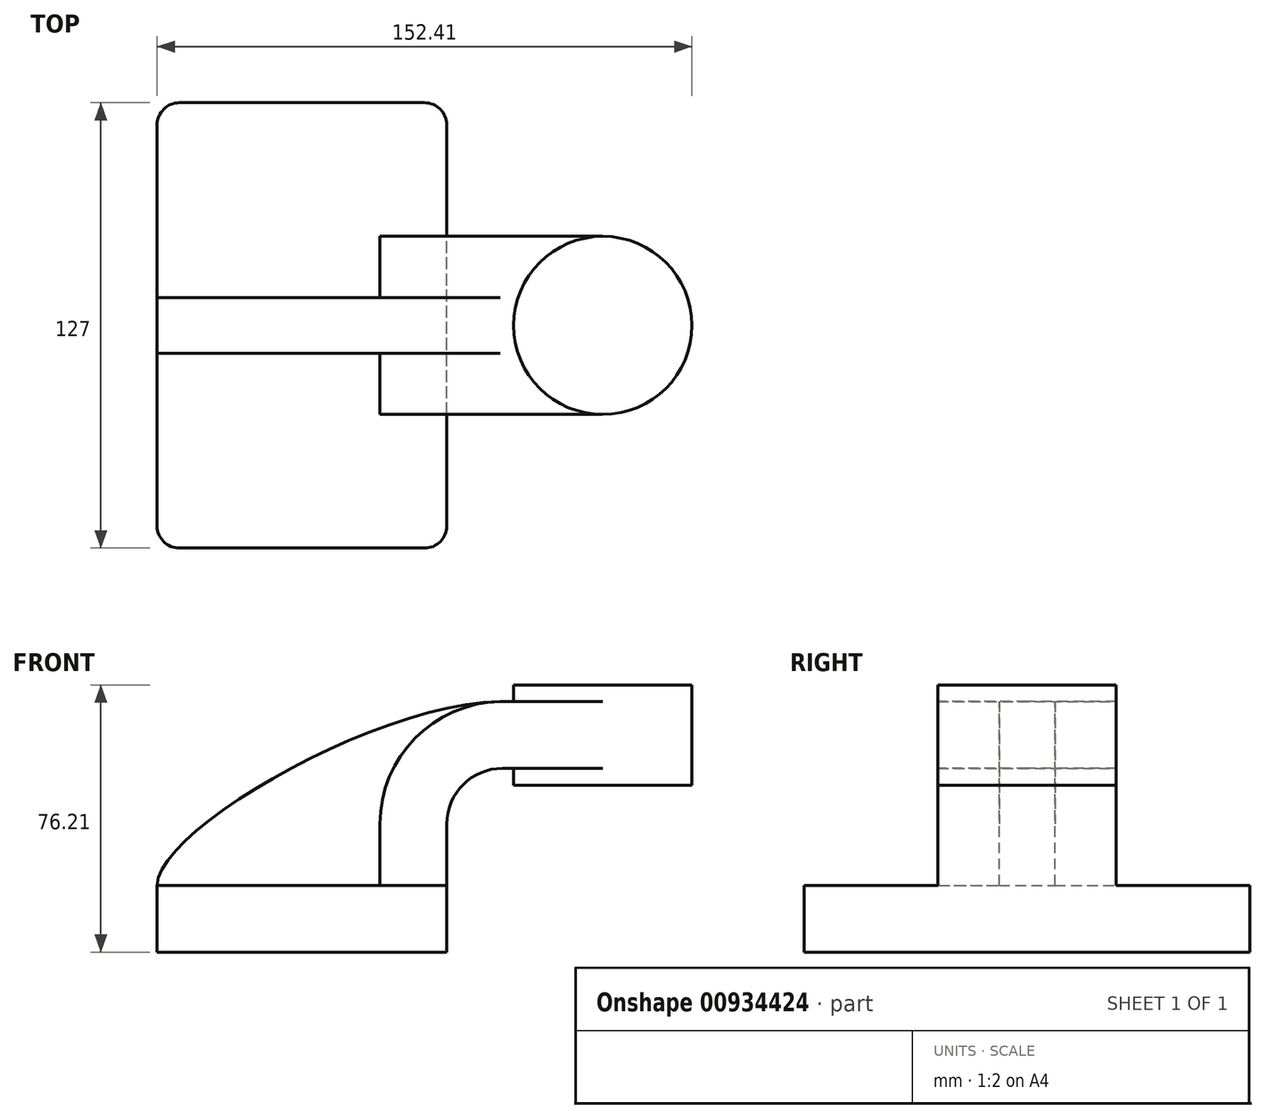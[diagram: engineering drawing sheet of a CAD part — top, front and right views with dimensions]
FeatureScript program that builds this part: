
annotation { "Feature Type Name" : "Feature", "Feature Type Description" : "" }
export const myFeature = defineFeature(function(context is Context, id is Id, definition is map)
    precondition{}
    {
        {
            var Q0;
            Q0=qCreatedBy(makeId("Front.planeOp"),FACE);
            var sketch = newSketch(context, id + "F0", { "sketchPlane" : qUnion([Q0])});
            skLineSegment(sketch, "E0.bottom", {"start": v(-41.28, 9.53) * mm, "end": v(41.27, 9.53) * mm});
            skLineSegment(sketch, "E0.top", {"start": v(-41.28, -9.53) * mm, "end": v(41.28, -9.53) * mm});
            skLineSegment(sketch, "E0.left", {"start": v(-41.27, 9.52) * mm, "end": v(-41.27, -9.53) * mm});
            skLineSegment(sketch, "E0.right", {"start": v(41.27, 9.53) * mm, "end": v(41.27, -9.52) * mm});
            skPoint(sketch, "E0.middle", {"position": v(0, 0) * mm});
            skLineSegment(sketch, "E1", {"start": v(41.28, 9.53) * mm, "end": v(41.28, 27) * mm});
            skArc(sketch, "E2", {"start": v(41.27, 27) * mm, "mid": v(45.92, 38.23) * mm, "end": v(57.15, 42.88) * mm});
            skLineSegment(sketch, "E3.bottom", {"start": v(111.12, 66.67) * mm, "end": v(60.32, 66.67) * mm});
            skLineSegment(sketch, "E3.top", {"start": v(111.12, 38.1) * mm, "end": v(60.32, 38.1) * mm});
            skLineSegment(sketch, "E3.left", {"start": v(111.12, 66.67) * mm, "end": v(111.12, 38.1) * mm});
            skLineSegment(sketch, "E3.right", {"start": v(60.32, 66.67) * mm, "end": v(60.32, 38.1) * mm});
            skPoint(sketch, "E3.middle", {"position": v(85.72, 52.39) * mm});
            skLineSegment(sketch, "E4", {"start": v(57.15, 42.88) * mm, "end": v(85.72, 42.88) * mm});
            skLineSegment(sketch, "E5.0", {"start": v(57.15, 61.93) * mm, "end": v(85.72, 61.93) * mm});
            skArc(sketch, "E5.1", {"start": v(22.22, 27) * mm, "mid": v(32.45, 51.7) * mm, "end": v(57.15, 61.93) * mm});
            skLineSegment(sketch, "E5.2", {"start": v(22.23, 9.53) * mm, "end": v(22.23, 27) * mm});
            skLineSegment(sketch, "E6", {"start": v(85.72, 38.1) * mm, "end": v(85.72, 66.67) * mm});
            skFitSpline(sketch, "E7", {"points": [v(-41.28, 9.52) * mm, v(57.15, 61.93) * mm], "startDerivative": vector(0.6, 47.75) * mm, "endDerivative": vector(106.9, 0.34) * mm});
            skSolve(sketch);
        }
        {
            var Q0;
            Q0=makeQuery(id+"F0.imprint","IMPRINT",FACE,{"disambiguationData":[TD([[makeQuery(id+"F0.imprint","IMPRINT",EDGE,{"derivedFrom":sQuery(id+"F0.wireOp",EDGE,"E0.top")}),1.0]])]});
            extrude(context, id + "F1", {"entities" : qUnion([Q0]), "endBound" : BoundingType.SYMMETRIC, "depth" : 127 * mm, "offsetDistance" : 25.4 * mm});
        }
        {
            var Q0;
            {var subQ5=sQuery(id+"F0.wireOp",EDGE,"E1");Q0=makeQuery(id+"F0.imprint","IMPRINT",FACE,{"disambiguationData":[TD([[makeQuery(id+"F0.imprint","IMPRINT",EDGE,{"derivedFrom":subQ5}),1.0]])]});}
            extrude(context, id + "F2", {"entities" : qUnion([Q0]), "operationType" : NewBodyOperationType.ADD, "endBound" : BoundingType.SYMMETRIC, "depth" : 50.8 * mm, "offsetDistance" : 25.4 * mm});
        }
        {
            var Q0;
            {var subQ0=sQuery(id+"F0.wireOp",EDGE,"E5.0");var subQ1=sQuery(id+"F0.wireOp",EDGE,"E3.right");var subQ2=makeQuery(id+"F0.imprint","INTERSECT",VERTEX,{"derivedFrom":[subQ1,subQ0]});Q0=makeQuery(id+"F0.imprint","IMPRINT",FACE,{"disambiguationData":[TD([[makeQuery(id+"F0.imprint","IMPRINT",EDGE,{"disambiguationData":[TD([[subQ2,-1.0]])],"derivedFrom":subQ1}),1.0]])]});}
            extrude(context, id + "F3", {"entities" : qUnion([Q0]), "operationType" : NewBodyOperationType.ADD, "endBound" : BoundingType.SYMMETRIC, "depth" : 50.8 * mm, "offsetDistance" : 25.4 * mm});
        }
        {
            var Q0;
            {var subQ3=sQuery(id+"F0.wireOp",EDGE,"E5.2");Q0=makeQuery(id+"F0.imprint","IMPRINT",FACE,{"disambiguationData":[TD([[makeQuery(id+"F0.imprint","IMPRINT",EDGE,{"derivedFrom":subQ3}),1.0]])]});}
            extrude(context, id + "F4", {"entities" : qUnion([Q0]), "operationType" : NewBodyOperationType.ADD, "endBound" : BoundingType.SYMMETRIC, "depth" : 15.88 * mm, "offsetDistance" : 25.4 * mm});
        }
        {
            var Q0;
            {var subQ0=sQuery(id+"F0.wireOp",EDGE,"E3.left");Q0=makeQuery(id+"F0.imprint","IMPRINT",FACE,{"disambiguationData":[TD([[makeQuery(id+"F0.imprint","IMPRINT",EDGE,{"derivedFrom":subQ0}),-1.0]])]});}
            var Q1;
            Q1=sQuery(id+"F0.wireOp",EDGE,"E6");
            revolve(context, id + "F5", {"operationType" : NewBodyOperationType.ADD, "surfaceOperationType" : NewSurfaceOperationType.NEW, "entities" : qUnion([Q0]), "axis" : qUnion([Q1]), "revolveType" : RevolveType.FULL});
        }
        {
            var Q0;
            Q0=makeQuery(id+"F1.opExtrude","CAP_EDGE",EDGE,{"disambiguationData":[OSD([sQuery(id+"F0.wireOp",EDGE,"E0.left")])],"isStart":false});
            var Q1;
            Q1=makeQuery(id+"F1.opExtrude","CAP_EDGE",EDGE,{"disambiguationData":[OSD([sQuery(id+"F0.wireOp",EDGE,"E0.right")])],"isStart":false});
            var Q2;
            Q2=makeQuery(id+"F1.opExtrude","CAP_EDGE",EDGE,{"disambiguationData":[OSD([sQuery(id+"F0.wireOp",EDGE,"E0.right")])],"isStart":true});
            var Q3;
            Q3=makeQuery(id+"F1.opExtrude","CAP_EDGE",EDGE,{"disambiguationData":[OSD([sQuery(id+"F0.wireOp",EDGE,"E0.left")])],"isStart":true});
            fillet(context, id + "F6", {"entities" : qUnion([Q0, Q1, Q2, Q3]), "radius" : 6.35 * mm, "tangentPropagation" : true, "allowEdgeOverflow" : false});
        }
    });
